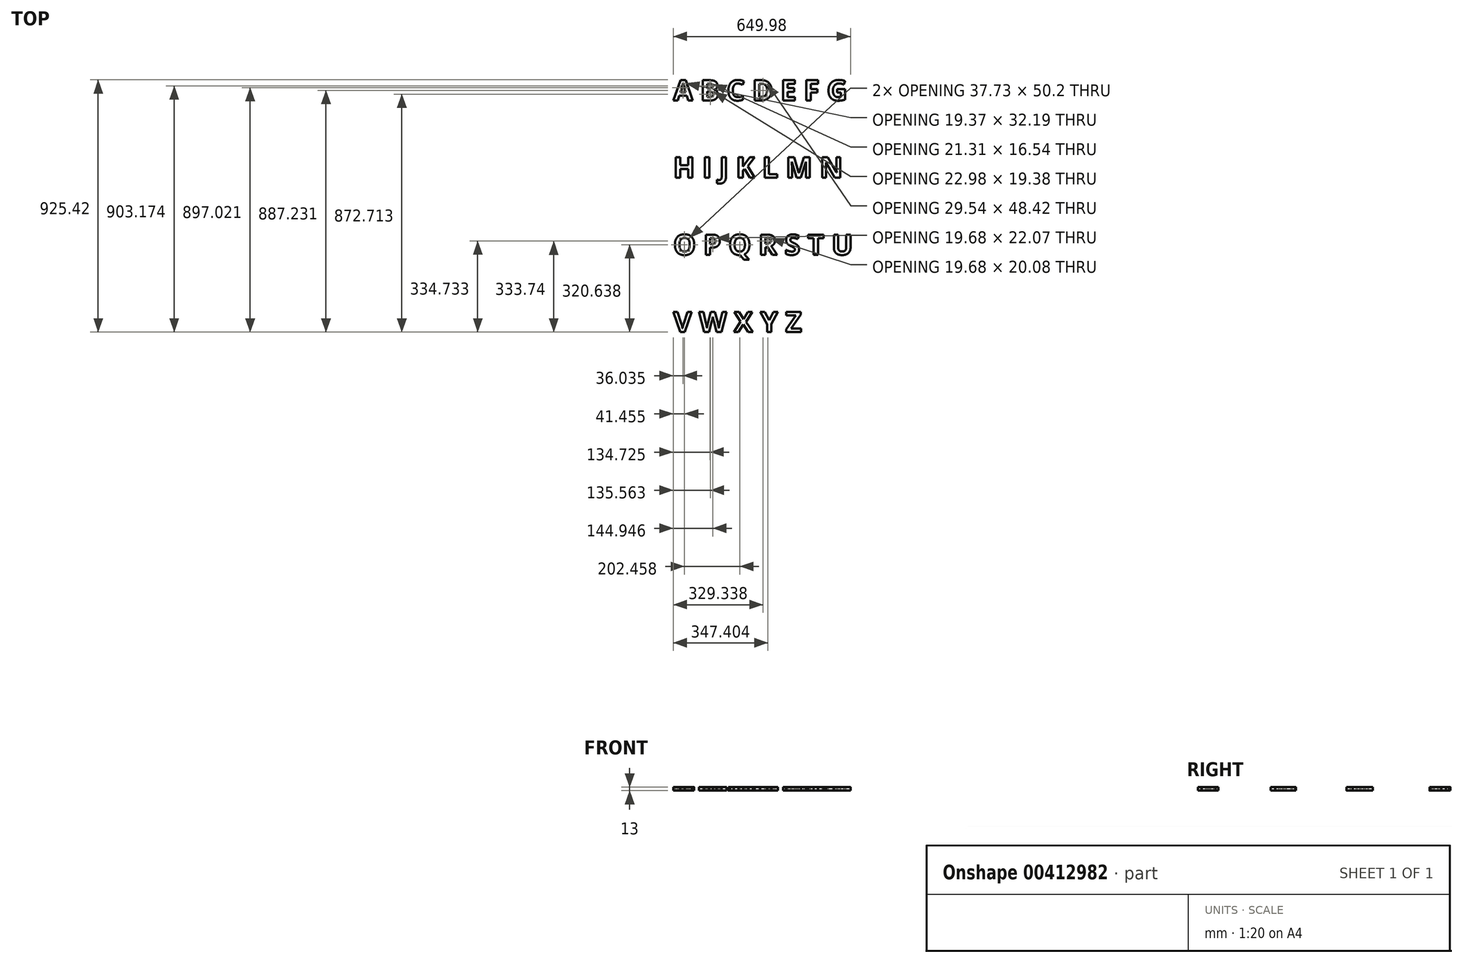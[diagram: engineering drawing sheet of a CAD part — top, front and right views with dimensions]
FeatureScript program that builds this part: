
annotation { "Feature Type Name" : "Feature", "Feature Type Description" : "" }
export const myFeature = defineFeature(function(context is Context, id is Id, definition is map)
    precondition{}
    {
        {
            var Q0;
            Q0=qCreatedBy(makeId("Top.planeOp"),FACE);
            var sketch = newSketch(context, id + "F0", { "sketchPlane" : qUnion([Q0])});
            skText(sketch, "E0", { "text": "A B C D E F G \n\nH I J K L M N\n\nO P Q R S T U\n\nV W X Y Z ", "fontName": "OpenSans-Bold.ttf"});
            const initialGuessF0  = {"E0": [-0.06653, -0.0375, 1, 0, 0.075]};
            skSetInitialGuess(sketch, initialGuessF0);
            skSolve(sketch);
        }
        {
            var Q0;
            Q0=qSketchRegion(id+"F0",true);
            extrude(context, id + "F1", {"entities" : qUnion([Q0]), "oppositeDirection" : true, "depth" : 13 * mm});
        }
    });
